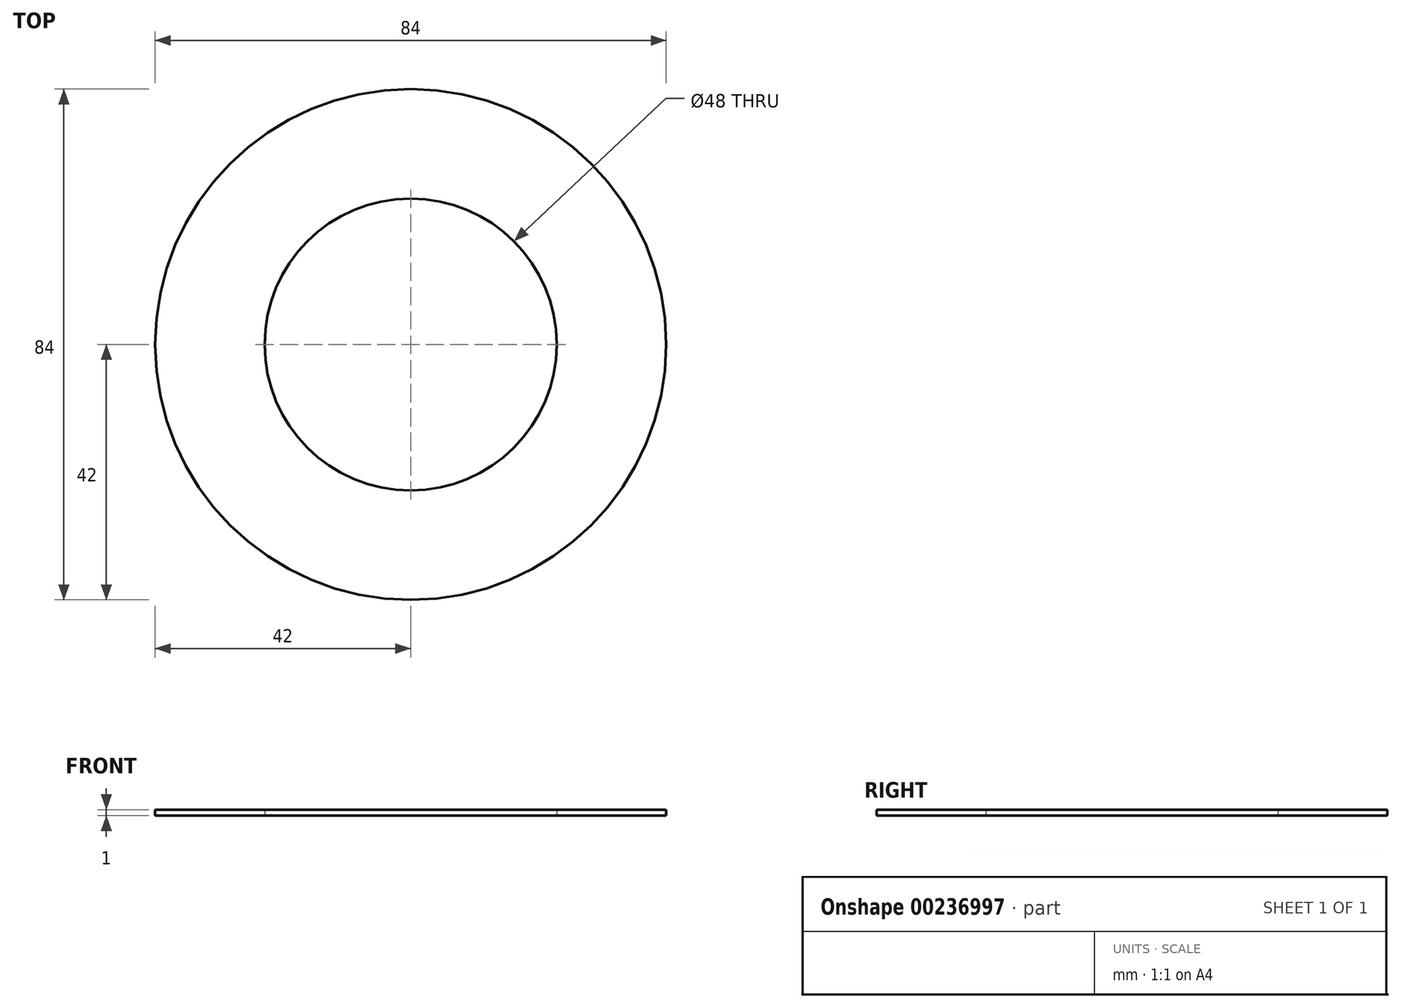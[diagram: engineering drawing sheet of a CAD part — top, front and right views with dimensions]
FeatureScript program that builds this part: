
annotation { "Feature Type Name" : "Feature", "Feature Type Description" : "" }
export const myFeature = defineFeature(function(context is Context, id is Id, definition is map)
    precondition{}
    {
        {
            var Q0;
            Q0=qCreatedBy(makeId("Top.planeOp"),FACE);
            var sketch = newSketch(context, id + "F0", { "sketchPlane" : qUnion([Q0])});
            skCircle(sketch, "E0", {"center": v(0, 0) * mm, "radius": 42 * mm});
            skCircle(sketch, "E1", {"center": v(0, 0) * mm, "radius": 24 * mm});
            skSolve(sketch);
        }
        {
            var Q0;
            Q0=makeQuery(id+"F0.imprint","IMPRINT",FACE,{"disambiguationData":[TD([[makeQuery(id+"F0.imprint","IMPRINT",EDGE,{"derivedFrom":sQuery(id+"F0.wireOp",EDGE,"E0")}),1.0]])]});
            extrude(context, id + "F1", {"entities" : qUnion([Q0]), "depth" : 1 * mm});
        }
    });
